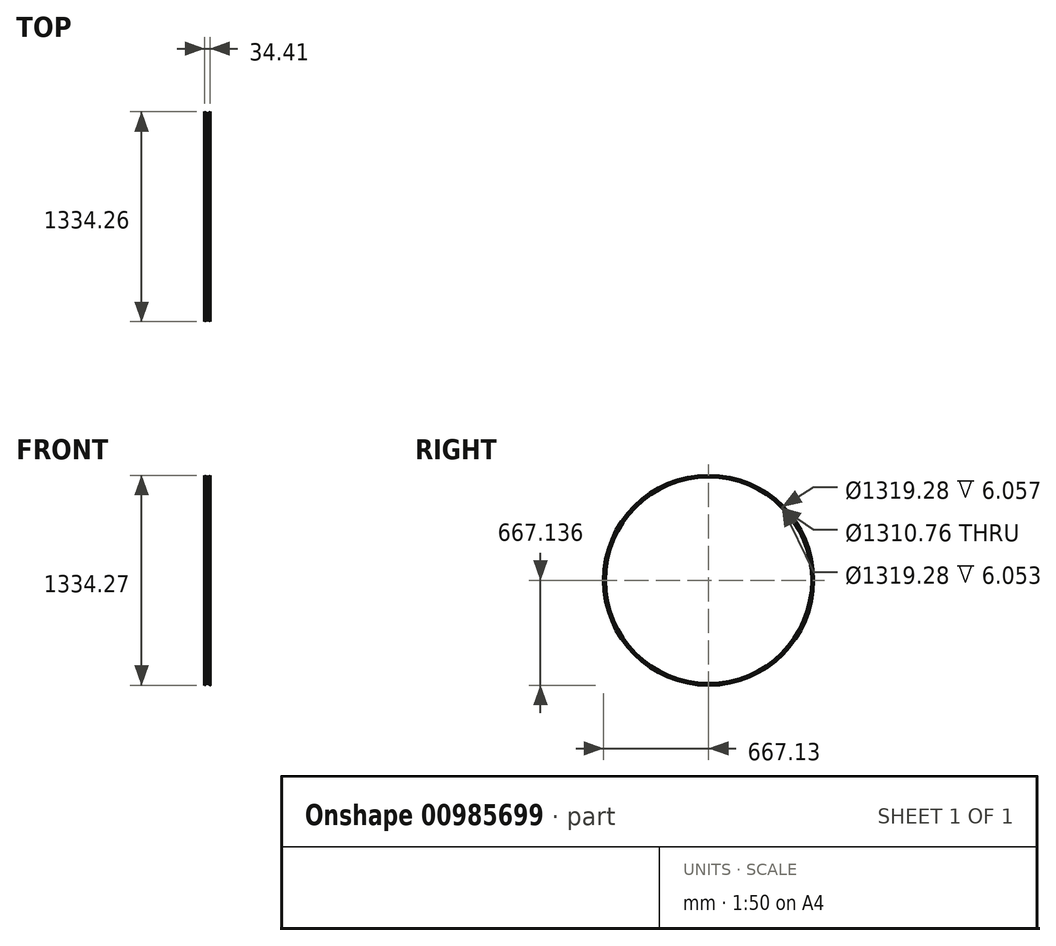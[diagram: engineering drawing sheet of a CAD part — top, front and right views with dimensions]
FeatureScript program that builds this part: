
annotation { "Feature Type Name" : "Feature", "Feature Type Description" : "" }
export const myFeature = defineFeature(function(context is Context, id is Id, definition is map)
    precondition{}
    {
        {
            var Q0;
            Q0=qCreatedBy(makeId("Front.planeOp"),FACE);
            var sketch = newSketch(context, id + "F0", { "sketchPlane" : qUnion([Q0])});
            skArc(sketch, "E0", {"start": v(11.64, -7.81) * mm, "mid": v(11.9, -13.37) * mm, "end": v(16.45, -10.16) * mm});
            skArc(sketch, "E1", {"start": v(-16.26, -9.38) * mm, "mid": v(-12.28, -13.53) * mm, "end": v(-11.64, -7.81) * mm});
            skFitSpline(sketch, "E2", {"points": [v(-16.47, -10.39) * mm, v(-16.8, -3.44) * mm, v(-34.3, 7.55) * mm], "startDerivative": vector(4.07, 19.24) * mm, "endDerivative": vector(-36.18, 16.85) * mm});
            skFitSpline(sketch, "E3", {"points": [v(16.47, -10.28) * mm, v(17.6, -2.46) * mm, v(30.94, 1.9) * mm], "startDerivative": vector(-1.93, 20.56) * mm, "endDerivative": vector(29.34, 4.55) * mm});
            skArc(sketch, "E4", {"start": v(11.64, -7.81) * mm, "mid": v(0, 33.35) * mm, "end": v(-11.64, -7.81) * mm});
            skArc(sketch, "E5", {"start": v(16.33, -5.77) * mm, "mid": v(-0.24, 34.62) * mm, "end": v(-15.97, -6.1) * mm});
            skSolve(sketch);
        }
        {
            var Q0;
            Q0=qCreatedBy(makeId("Front.planeOp"),FACE);
            var sketch = newSketch(context, id + "F1", { "sketchPlane" : qUnion([Q0])});
            skLineSegment(sketch, "E6", {"start": v(-16.47, -6.96) * mm, "end": v(-16.47, -13.7) * mm});
            skLineSegment(sketch, "E7", {"start": v(-16.47, -13.7) * mm, "end": v(-10.88, -13.7) * mm});
            skLineSegment(sketch, "E8", {"start": v(-10.88, -13.7) * mm, "end": v(-6.35, -17.95) * mm});
            skLineSegment(sketch, "E9", {"start": v(-6.35, -17.95) * mm, "end": v(6.35, -17.95) * mm});
            skLineSegment(sketch, "E10", {"start": v(6.35, -17.95) * mm, "end": v(10.8, -13.7) * mm});
            skLineSegment(sketch, "E11", {"start": v(10.8, -13.7) * mm, "end": v(16.4, -13.7) * mm});
            skLineSegment(sketch, "E12", {"start": v(16.4, -13.7) * mm, "end": v(16.4, -6.96) * mm});
            skLineSegment(sketch, "E13.0", {"start": v(17.17, -14.46) * mm, "end": v(17.17, -6.96) * mm});
            skLineSegment(sketch, "E13.1", {"start": v(11.12, -14.46) * mm, "end": v(17.17, -14.46) * mm});
            skLineSegment(sketch, "E13.2", {"start": v(6.66, -18.71) * mm, "end": v(11.12, -14.46) * mm});
            skLineSegment(sketch, "E13.3", {"start": v(-17.24, -6.96) * mm, "end": v(-17.24, -14.46) * mm});
            skLineSegment(sketch, "E13.4", {"start": v(-17.24, -14.46) * mm, "end": v(-11.18, -14.46) * mm});
            skLineSegment(sketch, "E13.5", {"start": v(-11.18, -14.46) * mm, "end": v(-6.65, -18.71) * mm});
            skLineSegment(sketch, "E13.6", {"start": v(-6.65, -18.71) * mm, "end": v(6.66, -18.71) * mm});
            skLineSegment(sketch, "E14", {"start": v(-17.24, -6.96) * mm, "end": v(-16.47, -6.96) * mm});
            skLineSegment(sketch, "E15", {"start": v(17.17, -6.96) * mm, "end": v(16.4, -6.96) * mm});
            skSolve(sketch);
        }
        {
            var Q0;
            Q0=qCreatedBy(makeId("Front.planeOp"),FACE);
            var sketch = newSketch(context, id + "F2", { "sketchPlane" : qUnion([Q0])});
            skLineSegment(sketch, "E16", {"start": v(827.86, -674.1) * mm, "end": v(-843.38, -674.1) * mm});
            skSolve(sketch);
        }
        {
            var Q0;
            Q0 = qSketchRegion(id + "F1", true);
            var Q1;
            Q1=sQuery(id+"F2.wireOp",EDGE,"E16");
            revolve(context, id + "F3", {"surfaceOperationType" : NewSurfaceOperationType.NEW, "entities" : qUnion([Q0]), "axis" : qUnion([Q1]), "revolveType" : RevolveType.FULL});
        }
    });
